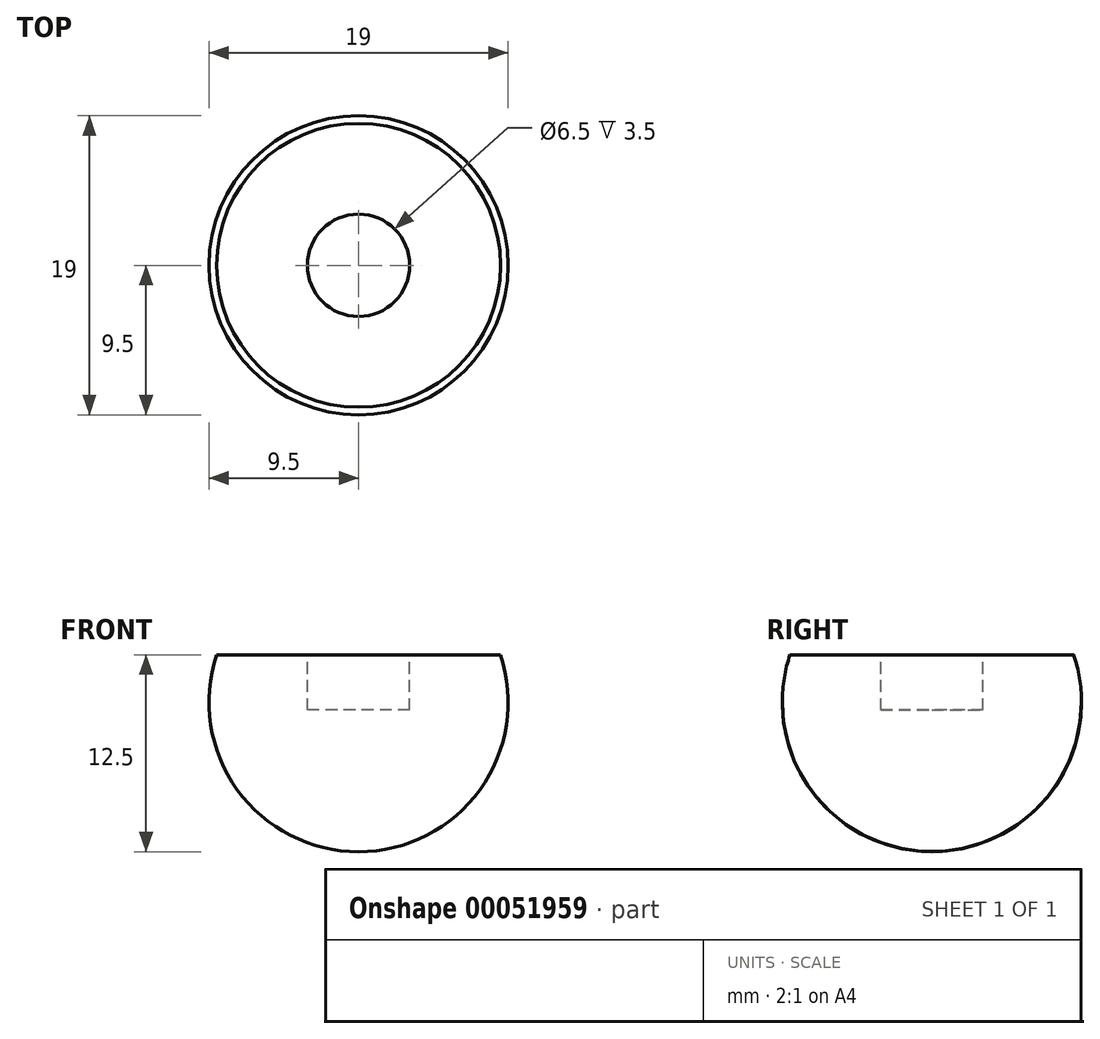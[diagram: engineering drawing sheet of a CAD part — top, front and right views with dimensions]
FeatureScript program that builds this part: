
annotation { "Feature Type Name" : "Feature", "Feature Type Description" : "" }
export const myFeature = defineFeature(function(context is Context, id is Id, definition is map)
    precondition{}
    {
        {
            var Q0;
            Q0=qCreatedBy(makeId("Right.planeOp"),FACE);
            var sketch = newSketch(context, id + "F0", { "sketchPlane" : qUnion([Q0])});
            skArc(sketch, "E0", {"start": v(-9.5, 0) * mm, "mid": v(0, -9.5) * mm, "end": v(9.5, 0) * mm});
            skLineSegment(sketch, "E1", {"start": v(-9.5, 0) * mm, "end": v(9.5, 0) * mm});
            skSolve(sketch);
        }
        {
            var Q0;
            Q0 = qSketchRegion(id + "F0", true);
            var Q1;
            Q1=sQuery(id+"F0.wireOp",EDGE,"E1");
            revolve(context, id + "F1", {"entities" : qUnion([Q0]), "axis" : qUnion([Q1]), "revolveType" : RevolveType.FULL});
        }
        {
            var Q0;
            Q0=qCreatedBy(makeId("Top.planeOp"),FACE);
            var sketch = newSketch(context, id + "F2", { "sketchPlane" : qUnion([Q0])});
            skLineSegment(sketch, "E2.rect.bottom", {"start": v(12.85, -12.3) * mm, "end": v(-12.85, -12.3) * mm});
            skLineSegment(sketch, "E2.rect.top", {"start": v(12.85, 12.3) * mm, "end": v(-12.85, 12.3) * mm});
            skLineSegment(sketch, "E2.rect.left", {"start": v(12.85, -12.3) * mm, "end": v(12.85, 12.3) * mm});
            skLineSegment(sketch, "E2.rect.right", {"start": v(-12.85, -12.3) * mm, "end": v(-12.85, 12.3) * mm});
            skPoint(sketch, "E2.rect.middle", {"position": v(0, 0) * mm});
            skSolve(sketch);
        }
        {
            var Q0;
            Q0 = qSketchRegion(id + "F2", true);
            extrude(context, id + "F3", {"entities" : qUnion([Q0]), "depth" : 25 * mm});
        }
        {
            var Q0;
            Q0=makeQuery(id+"F3.opExtrude","SWEPT_BODY",BODY,{"disambiguationData":[OSD([sQuery(id+"F2.wireOp",EDGE,"E2.rect.bottom"),sQuery(id+"F2.wireOp",EDGE,"E2.rect.top"),sQuery(id+"F2.wireOp",EDGE,"E2.rect.left"),sQuery(id+"F2.wireOp",EDGE,"E2.rect.right")])]});
            transform(context, id + "F4", {"entities" : qUnion([Q0]), "transformType" : TransformType.TRANSLATION_3D, "dx" : 0 * mm, "dy" : 0 * mm, "dz" : 3 * mm, "makeCopy" : false});
        }
        {
            var Q0;
            Q0=makeQuery(id+"F3.opExtrude","SWEPT_BODY",BODY,{"disambiguationData":[OSD([sQuery(id+"F2.wireOp",EDGE,"E2.rect.bottom"),sQuery(id+"F2.wireOp",EDGE,"E2.rect.top"),sQuery(id+"F2.wireOp",EDGE,"E2.rect.left"),sQuery(id+"F2.wireOp",EDGE,"E2.rect.right")])]});
            var Q1;
            Q1=makeQuery(id+"F1.opRevolve","SWEPT_BODY",BODY,{"disambiguationData":[OSD([sQuery(id+"F0.wireOp",EDGE,"E0"),sQuery(id+"F0.wireOp",EDGE,"E1")])]});
            booleanBodies(context, id + "F5", {"operationType" : BooleanOperationType.SUBTRACTION, "tools" : qUnion([Q0]), "targets" : qUnion([Q1])});
        }
        {
            var Q0;
            Q0=makeQuery(id+"F5.opBoolean","COPY",FACE,{"derivedFrom":makeQuery(id+"F3.opExtrude","CAP_FACE",FACE,{"disambiguationData":[OSD([sQuery(id+"F2.wireOp",EDGE,"E2.rect.bottom"),sQuery(id+"F2.wireOp",EDGE,"E2.rect.top"),sQuery(id+"F2.wireOp",EDGE,"E2.rect.left"),sQuery(id+"F2.wireOp",EDGE,"E2.rect.right")])],"isStart":true})});
            var sketch = newSketch(context, id + "F6", { "sketchPlane" : qUnion([Q0])});
            skCircle(sketch, "E3", {"center": v(0, 0) * mm, "radius": 3.25 * mm});
            skSolve(sketch);
        }
        {
            var Q0;
            Q0 = qSketchRegion(id + "F6", true);
            extrude(context, id + "F7", {"entities" : qUnion([Q0]), "operationType" : NewBodyOperationType.REMOVE, "oppositeDirection" : true, "depth" : 3.5 * mm});
        }
    });
